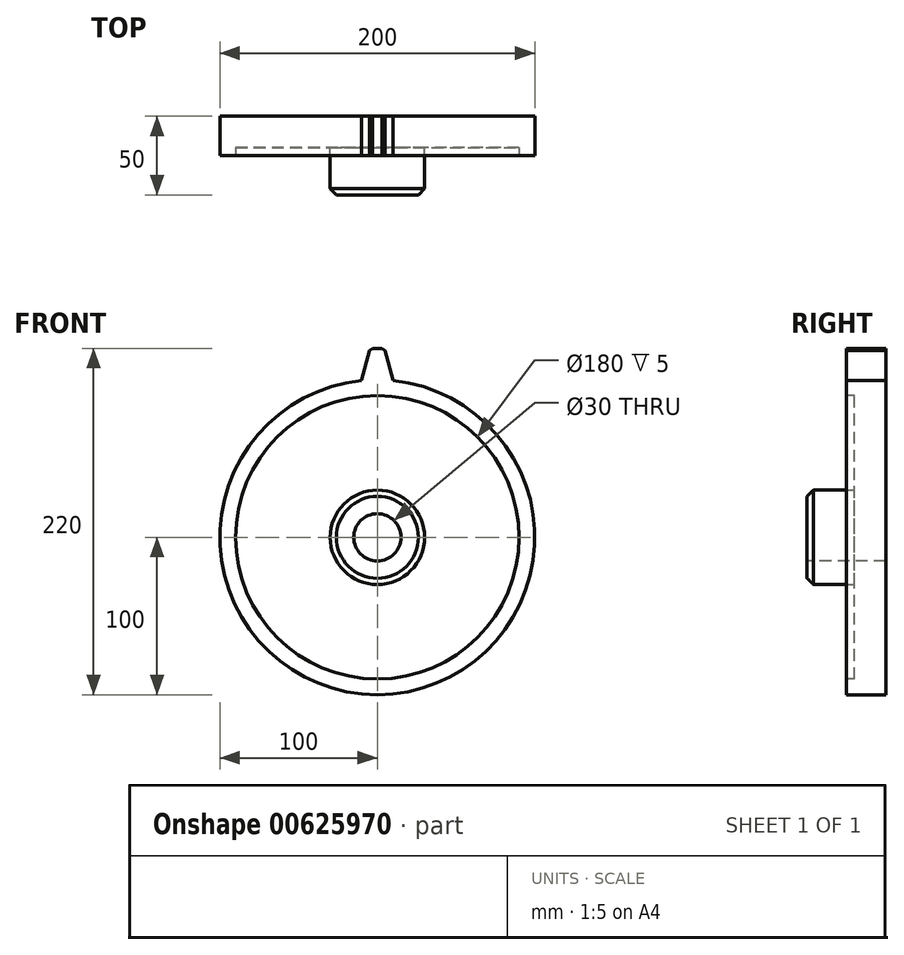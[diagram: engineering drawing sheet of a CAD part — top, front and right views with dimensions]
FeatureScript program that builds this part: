
annotation { "Feature Type Name" : "Feature", "Feature Type Description" : "" }
export const myFeature = defineFeature(function(context is Context, id is Id, definition is map)
    precondition{}
    {
        {
            var Q0;
            Q0=qCreatedBy(makeId("Front.planeOp"),FACE);
            var sketch = newSketch(context, id + "F0", { "sketchPlane" : qUnion([Q0])});
            skCircle(sketch, "E0", {"center": v(0, 0) * mm, "radius": 100 * mm});
            skSolve(sketch);
        }
        {
            var Q0;
            Q0 = qSketchRegion(id + "F0", true);
            extrude(context, id + "F1", {"entities" : qUnion([Q0]), "depth" : 25 * mm, "offsetDistance" : 25 * mm});
        }
        {
            var Q0;
            Q0=makeQuery(id+"F1.opExtrude","CAP_FACE",FACE,{"disambiguationData":[OSD([sQuery(id+"F0.wireOp",EDGE,"E0")])],"isStart":false});
            var sketch = newSketch(context, id + "F2", { "sketchPlane" : qUnion([Q0])});
            skLineSegment(sketch, "E1", {"start": v(-10, 99.5) * mm, "end": v(-4.5, 120) * mm});
            skLineSegment(sketch, "E2", {"start": v(-4.5, 120) * mm, "end": v(4.5, 120) * mm});
            skLineSegment(sketch, "E3", {"start": v(4.5, 120) * mm, "end": v(10, 99.5) * mm});
            skLineSegment(sketch, "E4", {"start": v(-10, 99.5) * mm, "end": v(10, 99.5) * mm});
            skSolve(sketch);
        }
        {
            var Q0;
            Q0 = qSketchRegion(id + "F2", true);
            extrude(context, id + "F3", {"entities" : qUnion([Q0]), "operationType" : NewBodyOperationType.ADD, "oppositeDirection" : true, "depth" : 25 * mm, "offsetDistance" : 25 * mm});
        }
        {
            var Q0;
            Q0=makeQuery(id+"F3.opExtrude","SWEPT_EDGE",EDGE,{"disambiguationData":[OSD([sQuery(id+"F0.wireOp",EDGE,"E0"),sQuery(id+"F2.wireOp",EDGE,"E3"),sQuery(id+"F2.wireOp",EDGE,"E4")])]});
            var Q1;
            Q1=makeQuery(id+"F3.opExtrude","SWEPT_EDGE",EDGE,{"disambiguationData":[OSD([sQuery(id+"F0.wireOp",EDGE,"E0"),sQuery(id+"F2.wireOp",EDGE,"E1"),sQuery(id+"F2.wireOp",EDGE,"E4")])]});
            fillet(context, id + "F4", {"entities" : qUnion([Q0, Q1]), "radius" : 5 * mm, "tangentPropagation" : true, "allowEdgeOverflow" : false});
        }
        {
            var Q0;
            Q0=makeQuery(id+"F3.opExtrude","SWEPT_EDGE",EDGE,{"disambiguationData":[OSD([sQuery(id+"F2.wireOp",EDGE,"E2"),sQuery(id+"F2.wireOp",EDGE,"E3")])]});
            var Q1;
            Q1=makeQuery(id+"F3.opExtrude","SWEPT_EDGE",EDGE,{"disambiguationData":[OSD([sQuery(id+"F2.wireOp",EDGE,"E1"),sQuery(id+"F2.wireOp",EDGE,"E2")])]});
            chamfer(context, id + "F5", {"entities" : qUnion([Q0, Q1]), "width" : 2 * mm, "tangentPropagation" : true});
        }
        {
            var Q0;
            {var subQ0=sQuery(id+"F2.wireOp",EDGE,"E4");var subQ1=sQuery(id+"F2.wireOp",EDGE,"E3");var subQ2=sQuery(id+"F2.wireOp",EDGE,"E2");var subQ3=sQuery(id+"F2.wireOp",EDGE,"E1");Q0=makeQuery(id+"FePQH3JD4Jeb5rY_1.19.F3.boolean.opBoolean","MERGE",FACE,{"derivedFrom":[makeQuery(id+"FePQH3JD4Jeb5rY_1.18.F3.boolean.opBoolean","MERGE",FACE,{"derivedFrom":[makeQuery(id+"FePQH3JD4Jeb5rY_1.17.F3.boolean.opBoolean","MERGE",FACE,{"derivedFrom":[makeQuery(id+"FePQH3JD4Jeb5rY_1.16.F3.boolean.opBoolean","MERGE",FACE,{"derivedFrom":[makeQuery(id+"FePQH3JD4Jeb5rY_1.15.F3.boolean.opBoolean","MERGE",FACE,{"derivedFrom":[makeQuery(id+"FePQH3JD4Jeb5rY_1.14.F3.boolean.opBoolean","MERGE",FACE,{"derivedFrom":[makeQuery(id+"FePQH3JD4Jeb5rY_1.13.F3.boolean.opBoolean","MERGE",FACE,{"derivedFrom":[makeQuery(id+"FePQH3JD4Jeb5rY_1.12.F3.boolean.opBoolean","MERGE",FACE,{"derivedFrom":[makeQuery(id+"FePQH3JD4Jeb5rY_1.11.F3.boolean.opBoolean","MERGE",FACE,{"derivedFrom":[makeQuery(id+"FePQH3JD4Jeb5rY_1.10.F3.boolean.opBoolean","MERGE",FACE,{"derivedFrom":[makeQuery(id+"FePQH3JD4Jeb5rY_1.9.F3.boolean.opBoolean","MERGE",FACE,{"derivedFrom":[makeQuery(id+"FePQH3JD4Jeb5rY_1.8.F3.boolean.opBoolean","MERGE",FACE,{"derivedFrom":[makeQuery(id+"FePQH3JD4Jeb5rY_1.7.F3.boolean.opBoolean","MERGE",FACE,{"derivedFrom":[makeQuery(id+"FePQH3JD4Jeb5rY_1.6.F3.boolean.opBoolean","MERGE",FACE,{"derivedFrom":[makeQuery(id+"FePQH3JD4Jeb5rY_1.5.F3.boolean.opBoolean","MERGE",FACE,{"derivedFrom":[makeQuery(id+"FePQH3JD4Jeb5rY_1.4.F3.boolean.opBoolean","MERGE",FACE,{"derivedFrom":[makeQuery(id+"FePQH3JD4Jeb5rY_1.3.F3.boolean.opBoolean","MERGE",FACE,{"derivedFrom":[makeQuery(id+"FePQH3JD4Jeb5rY_1.2.F3.boolean.opBoolean","MERGE",FACE,{"derivedFrom":[makeQuery(id+"FePQH3JD4Jeb5rY_1.1.F3.boolean.opBoolean","MERGE",FACE,{"derivedFrom":[makeQuery(id+"F3.boolean.opBoolean","MERGE",FACE,{"derivedFrom":[makeQuery(id+"F1.opExtrude","CAP_FACE",FACE,{"disambiguationData":[OSD([sQuery(id+"F0.wireOp",EDGE,"E0")])],"isStart":false}),makeQuery(id+"F3.opExtrude","CAP_FACE",FACE,{"disambiguationData":[OSD([subQ3,subQ2,subQ1,subQ0])],"isStart":true})]}),makeQuery(id+"FePQH3JD4Jeb5rY_1.1.F3.opExtrude","CAP_FACE",FACE,{"disambiguationData":[OSD([subQ3,subQ2,subQ1,subQ0])],"isStart":true})]}),makeQuery(id+"FePQH3JD4Jeb5rY_1.2.F3.opExtrude","CAP_FACE",FACE,{"disambiguationData":[OSD([subQ3,subQ2,subQ1,subQ0])],"isStart":true})]}),makeQuery(id+"FePQH3JD4Jeb5rY_1.3.F3.opExtrude","CAP_FACE",FACE,{"disambiguationData":[OSD([subQ3,subQ2,subQ1,subQ0])],"isStart":true})]}),makeQuery(id+"FePQH3JD4Jeb5rY_1.4.F3.opExtrude","CAP_FACE",FACE,{"disambiguationData":[OSD([subQ3,subQ2,subQ1,subQ0])],"isStart":true})]}),makeQuery(id+"FePQH3JD4Jeb5rY_1.5.F3.opExtrude","CAP_FACE",FACE,{"disambiguationData":[OSD([subQ3,subQ2,subQ1,subQ0])],"isStart":true})]}),makeQuery(id+"FePQH3JD4Jeb5rY_1.6.F3.opExtrude","CAP_FACE",FACE,{"disambiguationData":[OSD([subQ3,subQ2,subQ1,subQ0])],"isStart":true})]}),makeQuery(id+"FePQH3JD4Jeb5rY_1.7.F3.opExtrude","CAP_FACE",FACE,{"disambiguationData":[OSD([subQ3,subQ2,subQ1,subQ0])],"isStart":true})]}),makeQuery(id+"FePQH3JD4Jeb5rY_1.8.F3.opExtrude","CAP_FACE",FACE,{"disambiguationData":[OSD([subQ3,subQ2,subQ1,subQ0])],"isStart":true})]}),makeQuery(id+"FePQH3JD4Jeb5rY_1.9.F3.opExtrude","CAP_FACE",FACE,{"disambiguationData":[OSD([subQ3,subQ2,subQ1,subQ0])],"isStart":true})]}),makeQuery(id+"FePQH3JD4Jeb5rY_1.10.F3.opExtrude","CAP_FACE",FACE,{"disambiguationData":[OSD([subQ3,subQ2,subQ1,subQ0])],"isStart":true})]}),makeQuery(id+"FePQH3JD4Jeb5rY_1.11.F3.opExtrude","CAP_FACE",FACE,{"disambiguationData":[OSD([subQ3,subQ2,subQ1,subQ0])],"isStart":true})]}),makeQuery(id+"FePQH3JD4Jeb5rY_1.12.F3.opExtrude","CAP_FACE",FACE,{"disambiguationData":[OSD([subQ3,subQ2,subQ1,subQ0])],"isStart":true})]}),makeQuery(id+"FePQH3JD4Jeb5rY_1.13.F3.opExtrude","CAP_FACE",FACE,{"disambiguationData":[OSD([subQ3,subQ2,subQ1,subQ0])],"isStart":true})]}),makeQuery(id+"FePQH3JD4Jeb5rY_1.14.F3.opExtrude","CAP_FACE",FACE,{"disambiguationData":[OSD([subQ3,subQ2,subQ1,subQ0])],"isStart":true})]}),makeQuery(id+"FePQH3JD4Jeb5rY_1.15.F3.opExtrude","CAP_FACE",FACE,{"disambiguationData":[OSD([subQ3,subQ2,subQ1,subQ0])],"isStart":true})]}),makeQuery(id+"FePQH3JD4Jeb5rY_1.16.F3.opExtrude","CAP_FACE",FACE,{"disambiguationData":[OSD([subQ3,subQ2,subQ1,subQ0])],"isStart":true})]}),makeQuery(id+"FePQH3JD4Jeb5rY_1.17.F3.opExtrude","CAP_FACE",FACE,{"disambiguationData":[OSD([subQ3,subQ2,subQ1,subQ0])],"isStart":true})]}),makeQuery(id+"FePQH3JD4Jeb5rY_1.18.F3.opExtrude","CAP_FACE",FACE,{"disambiguationData":[OSD([subQ3,subQ2,subQ1,subQ0])],"isStart":true})]}),makeQuery(id+"FePQH3JD4Jeb5rY_1.19.F3.opExtrude","CAP_FACE",FACE,{"disambiguationData":[OSD([subQ3,subQ2,subQ1,subQ0])],"isStart":true})]});}
            var sketch = newSketch(context, id + "F6", { "sketchPlane" : qUnion([Q0])});
            skCircle(sketch, "E5", {"center": v(0, 0) * mm, "radius": 90 * mm});
            skSolve(sketch);
        }
        {
            var Q0;
            Q0 = qSketchRegion(id + "F6", true);
            extrude(context, id + "F7", {"entities" : qUnion([Q0]), "operationType" : NewBodyOperationType.REMOVE, "oppositeDirection" : true, "depth" : 5 * mm, "offsetDistance" : 25 * mm});
        }
        {
            var Q0;
            Q0=makeQuery(id+"F7.boolean.opBoolean","COPY",FACE,{"derivedFrom":makeQuery(id+"F7.opExtrude","CAP_FACE",FACE,{"disambiguationData":[OSD([sQuery(id+"F6.wireOp",EDGE,"E5")])],"isStart":false})});
            var sketch = newSketch(context, id + "F8", { "sketchPlane" : qUnion([Q0])});
            skCircle(sketch, "E6", {"center": v(0, 0) * mm, "radius": 30 * mm});
            skSolve(sketch);
        }
        {
            var Q0;
            Q0=makeQuery(id+"F8.imprint","IMPRINT",FACE,{"disambiguationData":[TD([[makeQuery(id+"F8.imprint","IMPRINT",EDGE,{"derivedFrom":sQuery(id+"F8.wireOp",EDGE,"E6")}),1.0]])]});
            extrude(context, id + "F9", {"entities" : qUnion([Q0]), "operationType" : NewBodyOperationType.ADD, "depth" : 30 * mm, "offsetDistance" : 25 * mm});
        }
        {
            var Q0;
            Q0=makeQuery(id+"F9.opExtrude","CAP_FACE",FACE,{"disambiguationData":[OSD([sQuery(id+"F8.wireOp",EDGE,"E6")])],"isStart":false});
            var sketch = newSketch(context, id + "F10", { "sketchPlane" : qUnion([Q0])});
            skCircle(sketch, "E7", {"center": v(0, 0) * mm, "radius": 15 * mm});
            skSolve(sketch);
        }
        {
            var Q0;
            Q0 = qSketchRegion(id + "F10", true);
            var Q1;
            {var subQ0=sQuery(id+"F2.wireOp",EDGE,"E4");var subQ1=sQuery(id+"F2.wireOp",EDGE,"E3");var subQ2=sQuery(id+"F2.wireOp",EDGE,"E2");var subQ3=sQuery(id+"F2.wireOp",EDGE,"E1");Q1=makeQuery(id+"FePQH3JD4Jeb5rY_1.19.F3.boolean.opBoolean","MERGE",FACE,{"derivedFrom":[makeQuery(id+"FePQH3JD4Jeb5rY_1.18.F3.boolean.opBoolean","MERGE",FACE,{"derivedFrom":[makeQuery(id+"FePQH3JD4Jeb5rY_1.17.F3.boolean.opBoolean","MERGE",FACE,{"derivedFrom":[makeQuery(id+"FePQH3JD4Jeb5rY_1.16.F3.boolean.opBoolean","MERGE",FACE,{"derivedFrom":[makeQuery(id+"FePQH3JD4Jeb5rY_1.15.F3.boolean.opBoolean","MERGE",FACE,{"derivedFrom":[makeQuery(id+"FePQH3JD4Jeb5rY_1.14.F3.boolean.opBoolean","MERGE",FACE,{"derivedFrom":[makeQuery(id+"FePQH3JD4Jeb5rY_1.13.F3.boolean.opBoolean","MERGE",FACE,{"derivedFrom":[makeQuery(id+"FePQH3JD4Jeb5rY_1.12.F3.boolean.opBoolean","MERGE",FACE,{"derivedFrom":[makeQuery(id+"FePQH3JD4Jeb5rY_1.11.F3.boolean.opBoolean","MERGE",FACE,{"derivedFrom":[makeQuery(id+"FePQH3JD4Jeb5rY_1.10.F3.boolean.opBoolean","MERGE",FACE,{"derivedFrom":[makeQuery(id+"FePQH3JD4Jeb5rY_1.9.F3.boolean.opBoolean","MERGE",FACE,{"derivedFrom":[makeQuery(id+"FePQH3JD4Jeb5rY_1.8.F3.boolean.opBoolean","MERGE",FACE,{"derivedFrom":[makeQuery(id+"FePQH3JD4Jeb5rY_1.7.F3.boolean.opBoolean","MERGE",FACE,{"derivedFrom":[makeQuery(id+"FePQH3JD4Jeb5rY_1.6.F3.boolean.opBoolean","MERGE",FACE,{"derivedFrom":[makeQuery(id+"FePQH3JD4Jeb5rY_1.5.F3.boolean.opBoolean","MERGE",FACE,{"derivedFrom":[makeQuery(id+"FePQH3JD4Jeb5rY_1.4.F3.boolean.opBoolean","MERGE",FACE,{"derivedFrom":[makeQuery(id+"FePQH3JD4Jeb5rY_1.3.F3.boolean.opBoolean","MERGE",FACE,{"derivedFrom":[makeQuery(id+"FePQH3JD4Jeb5rY_1.2.F3.boolean.opBoolean","MERGE",FACE,{"derivedFrom":[makeQuery(id+"FePQH3JD4Jeb5rY_1.1.F3.boolean.opBoolean","MERGE",FACE,{"derivedFrom":[makeQuery(id+"F3.boolean.opBoolean","MERGE",FACE,{"derivedFrom":[makeQuery(id+"F1.opExtrude","CAP_FACE",FACE,{"disambiguationData":[OSD([sQuery(id+"F0.wireOp",EDGE,"E0")])],"isStart":true}),makeQuery(id+"F3.opExtrude","CAP_FACE",FACE,{"disambiguationData":[OSD([subQ3,subQ2,subQ1,subQ0])],"isStart":false})]}),makeQuery(id+"FePQH3JD4Jeb5rY_1.1.F3.opExtrude","CAP_FACE",FACE,{"disambiguationData":[OSD([subQ3,subQ2,subQ1,subQ0])],"isStart":false})]}),makeQuery(id+"FePQH3JD4Jeb5rY_1.2.F3.opExtrude","CAP_FACE",FACE,{"disambiguationData":[OSD([subQ3,subQ2,subQ1,subQ0])],"isStart":false})]}),makeQuery(id+"FePQH3JD4Jeb5rY_1.3.F3.opExtrude","CAP_FACE",FACE,{"disambiguationData":[OSD([subQ3,subQ2,subQ1,subQ0])],"isStart":false})]}),makeQuery(id+"FePQH3JD4Jeb5rY_1.4.F3.opExtrude","CAP_FACE",FACE,{"disambiguationData":[OSD([subQ3,subQ2,subQ1,subQ0])],"isStart":false})]}),makeQuery(id+"FePQH3JD4Jeb5rY_1.5.F3.opExtrude","CAP_FACE",FACE,{"disambiguationData":[OSD([subQ3,subQ2,subQ1,subQ0])],"isStart":false})]}),makeQuery(id+"FePQH3JD4Jeb5rY_1.6.F3.opExtrude","CAP_FACE",FACE,{"disambiguationData":[OSD([subQ3,subQ2,subQ1,subQ0])],"isStart":false})]}),makeQuery(id+"FePQH3JD4Jeb5rY_1.7.F3.opExtrude","CAP_FACE",FACE,{"disambiguationData":[OSD([subQ3,subQ2,subQ1,subQ0])],"isStart":false})]}),makeQuery(id+"FePQH3JD4Jeb5rY_1.8.F3.opExtrude","CAP_FACE",FACE,{"disambiguationData":[OSD([subQ3,subQ2,subQ1,subQ0])],"isStart":false})]}),makeQuery(id+"FePQH3JD4Jeb5rY_1.9.F3.opExtrude","CAP_FACE",FACE,{"disambiguationData":[OSD([subQ3,subQ2,subQ1,subQ0])],"isStart":false})]}),makeQuery(id+"FePQH3JD4Jeb5rY_1.10.F3.opExtrude","CAP_FACE",FACE,{"disambiguationData":[OSD([subQ3,subQ2,subQ1,subQ0])],"isStart":false})]}),makeQuery(id+"FePQH3JD4Jeb5rY_1.11.F3.opExtrude","CAP_FACE",FACE,{"disambiguationData":[OSD([subQ3,subQ2,subQ1,subQ0])],"isStart":false})]}),makeQuery(id+"FePQH3JD4Jeb5rY_1.12.F3.opExtrude","CAP_FACE",FACE,{"disambiguationData":[OSD([subQ3,subQ2,subQ1,subQ0])],"isStart":false})]}),makeQuery(id+"FePQH3JD4Jeb5rY_1.13.F3.opExtrude","CAP_FACE",FACE,{"disambiguationData":[OSD([subQ3,subQ2,subQ1,subQ0])],"isStart":false})]}),makeQuery(id+"FePQH3JD4Jeb5rY_1.14.F3.opExtrude","CAP_FACE",FACE,{"disambiguationData":[OSD([subQ3,subQ2,subQ1,subQ0])],"isStart":false})]}),makeQuery(id+"FePQH3JD4Jeb5rY_1.15.F3.opExtrude","CAP_FACE",FACE,{"disambiguationData":[OSD([subQ3,subQ2,subQ1,subQ0])],"isStart":false})]}),makeQuery(id+"FePQH3JD4Jeb5rY_1.16.F3.opExtrude","CAP_FACE",FACE,{"disambiguationData":[OSD([subQ3,subQ2,subQ1,subQ0])],"isStart":false})]}),makeQuery(id+"FePQH3JD4Jeb5rY_1.17.F3.opExtrude","CAP_FACE",FACE,{"disambiguationData":[OSD([subQ3,subQ2,subQ1,subQ0])],"isStart":false})]}),makeQuery(id+"FePQH3JD4Jeb5rY_1.18.F3.opExtrude","CAP_FACE",FACE,{"disambiguationData":[OSD([subQ3,subQ2,subQ1,subQ0])],"isStart":false})]}),makeQuery(id+"FePQH3JD4Jeb5rY_1.19.F3.opExtrude","CAP_FACE",FACE,{"disambiguationData":[OSD([subQ3,subQ2,subQ1,subQ0])],"isStart":false})]});}
            extrude(context, id + "F11", {"entities" : qUnion([Q0, Q1]), "operationType" : NewBodyOperationType.REMOVE, "endBound" : BoundingType.THROUGH_ALL, "oppositeDirection" : true, "depth" : 25 * mm, "offsetDistance" : 25 * mm});
        }
        {
            var Q0;
            Q0=makeQuery(id+"F11.boolean.opBoolean","COPY",EDGE,{"derivedFrom":makeQuery(id+"F11.opExtrude","CAP_EDGE",EDGE,{"disambiguationData":[OSD([sQuery(id+"F10.wireOp",EDGE,"E7")])],"isStart":true})});
            var Q1;
            Q1=makeQuery(id+"F9.opExtrude","CAP_EDGE",EDGE,{"disambiguationData":[OSD([sQuery(id+"F8.wireOp",EDGE,"E6")])],"isStart":false});
            chamfer(context, id + "F12", {"entities" : qUnion([Q0, Q1]), "width" : 4 * mm, "tangentPropagation" : true});
        }
    });
